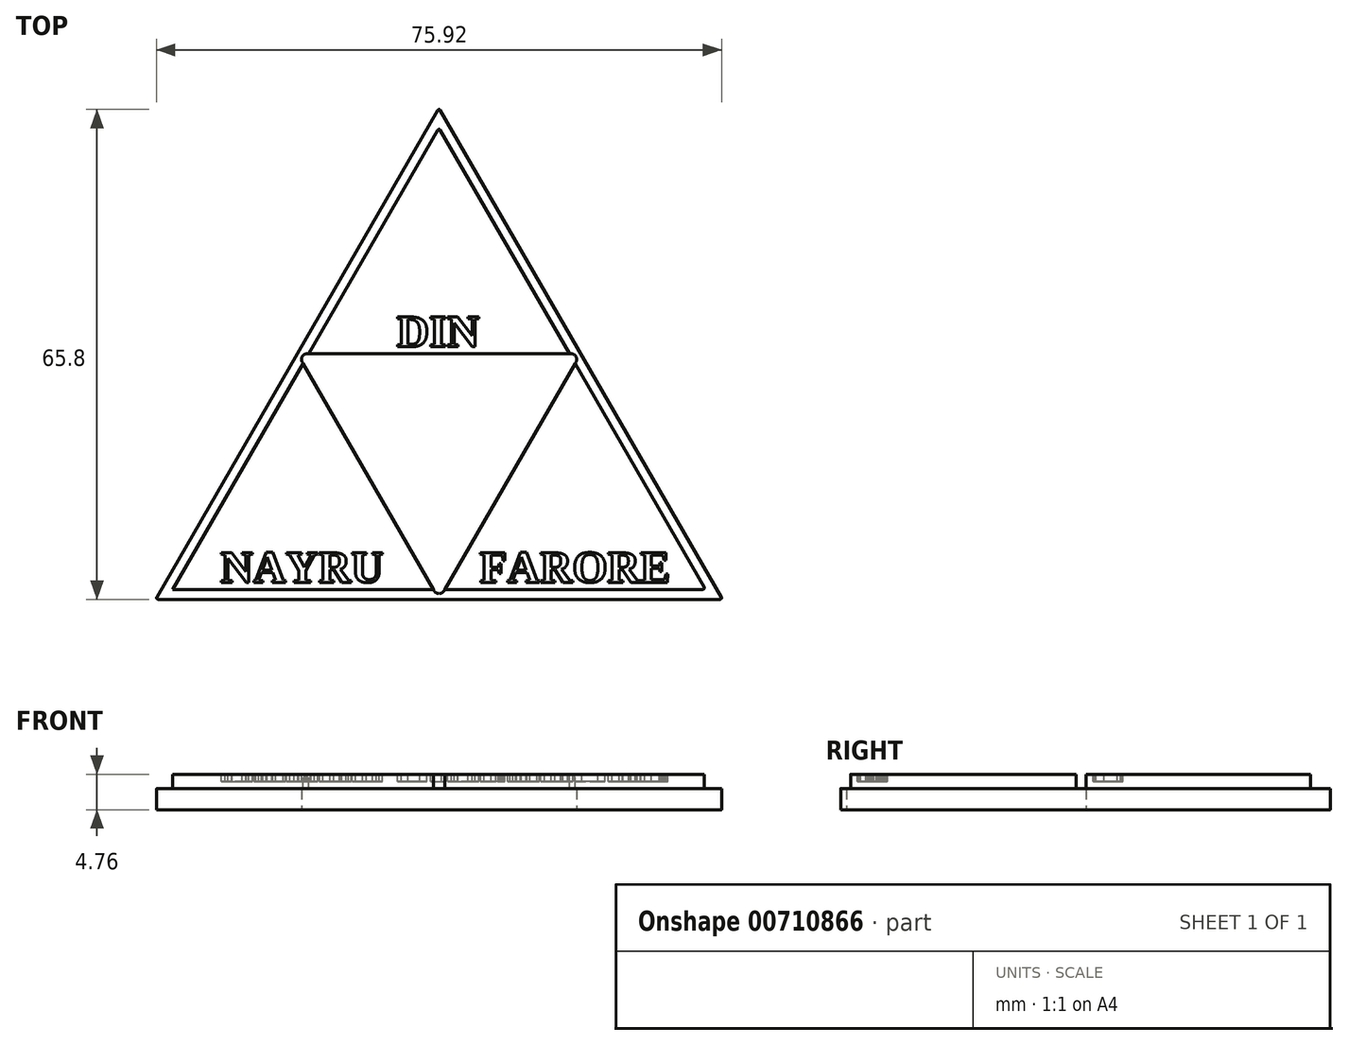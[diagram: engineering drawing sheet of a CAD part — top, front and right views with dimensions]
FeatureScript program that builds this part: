
annotation { "Feature Type Name" : "Feature", "Feature Type Description" : "" }
export const myFeature = defineFeature(function(context is Context, id is Id, definition is map)
    precondition{}
    {
        {
            var Q0;
            Q0=qCreatedBy(makeId("Top.planeOp"),FACE);
            var sketch = newSketch(context, id + "F0", { "sketchPlane" : qUnion([Q0])});
            skLineSegment(sketch, "E0", {"start": v(-0.1, -0.2) * mm, "end": v(-12.7, -22) * mm});
            skLineSegment(sketch, "E1", {"start": v(-11.82, -22) * mm, "end": v(11.82, -22) * mm});
            skLineSegment(sketch, "E2", {"start": v(12.7, -22) * mm, "end": v(0.1, -0.2) * mm});
            skLineSegment(sketch, "E3", {"start": v(-12.7, -22) * mm, "end": v(-25.3, -43.8) * mm});
            skLineSegment(sketch, "E4", {"start": v(-25.18, -44) * mm, "end": v(0, -44) * mm});
            skLineSegment(sketch, "E5", {"start": v(-0.44, -43.23) * mm, "end": v(-12.26, -22.76) * mm});
            skLineSegment(sketch, "E6", {"start": v(0.44, -43.23) * mm, "end": v(12.26, -22.76) * mm});
            skLineSegment(sketch, "E7", {"start": v(25.3, -43.8) * mm, "end": v(12.7, -22) * mm});
            skLineSegment(sketch, "E8", {"start": v(0, -44) * mm, "end": v(25.18, -44) * mm});
            skPoint(sketch, "E9.visualSharp", {"position": v(-12.7, -22) * mm});
            skArc(sketch, "E9.filletArc", {"start": v(-11.82, -22) * mm, "mid": v(-12.26, -22.25) * mm, "end": v(-12.26, -22.76) * mm});
            skPoint(sketch, "E10.visualSharp", {"position": v(12.7, -22) * mm});
            skArc(sketch, "E10.filletArc", {"start": v(12.26, -22.76) * mm, "mid": v(12.26, -22.25) * mm, "end": v(11.82, -22) * mm});
            skPoint(sketch, "E11.visualSharp", {"position": v(0, -44) * mm});
            skArc(sketch, "E11.filletArc", {"start": v(-0.44, -43.23) * mm, "mid": v(0, -43.49) * mm, "end": v(0.44, -43.23) * mm});
            skPoint(sketch, "E12.visualSharp", {"position": v(0, 0) * mm});
            skArc(sketch, "E12.filletArc", {"start": v(0.01, -0.02) * mm, "mid": v(0, -0.01) * mm, "end": v(-0.01, -0.02) * mm});
            skPoint(sketch, "E13.visualSharp", {"position": v(25.4, -44) * mm});
            skArc(sketch, "E13.filletArc", {"start": v(25.18, -44) * mm, "mid": v(25.3, -43.93) * mm, "end": v(25.3, -43.8) * mm});
            skPoint(sketch, "E14.visualSharp", {"position": v(-25.4, -44) * mm});
            skArc(sketch, "E14.filletArc", {"start": v(-25.3, -43.8) * mm, "mid": v(-25.3, -43.93) * mm, "end": v(-25.18, -44) * mm});
            skArc(sketch, "E15.filletArc", {"start": v(0.1, -0.2) * mm, "mid": v(0, -0.13) * mm, "end": v(-0.1, -0.2) * mm});
            skSolve(sketch);
        }
        {
            var Q0;
            Q0=makeQuery(id+"F0.imprint","IMPRINT",FACE,{"disambiguationData":[TD([[makeQuery(id+"F0.imprint","IMPRINT",EDGE,{"derivedFrom":sQuery(id+"F0.wireOp",EDGE,"E0")}),1.0]])]});
            var Q1;
            Q1=makeQuery(id+"F0.imprint","IMPRINT",FACE,{"disambiguationData":[TD([[makeQuery(id+"F0.imprint","IMPRINT",EDGE,{"derivedFrom":sQuery(id+"F0.wireOp",EDGE,"E6")}),-1.0]])]});
            var Q2;
            Q2=makeQuery(id+"F0.imprint","IMPRINT",FACE,{"disambiguationData":[TD([[makeQuery(id+"F0.imprint","IMPRINT",EDGE,{"derivedFrom":sQuery(id+"F0.wireOp",EDGE,"E3")}),1.0]])]});
            extrude(context, id + "F1", {"entities" : qUnion([Q0, Q1, Q2]), "depth" : 3.17 * mm, "offsetDistance" : 25.4 * mm});
        }
        {
            var Q0;
            Q0=makeQuery(id+"F1.opExtrude","CAP_FACE",FACE,{"disambiguationData":[OSD([sQuery(id+"F0.wireOp",EDGE,"E0"),sQuery(id+"F0.wireOp",EDGE,"E1"),sQuery(id+"F0.wireOp",EDGE,"E2"),sQuery(id+"F0.wireOp",EDGE,"E3"),sQuery(id+"F0.wireOp",EDGE,"E4"),sQuery(id+"F0.wireOp",EDGE,"E5"),sQuery(id+"F0.wireOp",EDGE,"E6"),sQuery(id+"F0.wireOp",EDGE,"E7"),sQuery(id+"F0.wireOp",EDGE,"E8"),sQuery(id+"F0.wireOp",EDGE,"E9.filletArc"),sQuery(id+"F0.wireOp",EDGE,"E10.filletArc"),sQuery(id+"F0.wireOp",EDGE,"E11.filletArc"),sQuery(id+"F0.wireOp",EDGE,"E13.filletArc"),sQuery(id+"F0.wireOp",EDGE,"E14.filletArc"),sQuery(id+"F0.wireOp",EDGE,"E15.filletArc")])],"isStart":false});
            var sketch = newSketch(context, id + "F2", { "sketchPlane" : qUnion([Q0])});
            skLineSegment(sketch, "E16", {"start": v(0, 0) * mm, "end": v(-25.4, -44) * mm});
            skLineSegment(sketch, "E17", {"start": v(0, 0) * mm, "end": v(25.4, -44) * mm});
            skLineSegment(sketch, "E18", {"start": v(25.18, -44) * mm, "end": v(25.4, -44) * mm});
            skLineSegment(sketch, "E19.trimOffspring", {"start": v(25.4, -44) * mm, "end": v(-25.4, -44) * mm});
            skLineSegment(sketch, "E20.0", {"start": v(-23.64, -43.1) * mm, "end": v(23.64, -43.1) * mm});
            skLineSegment(sketch, "E20.1", {"start": v(-0.1, -1.97) * mm, "end": v(-23.75, -42.91) * mm});
            skLineSegment(sketch, "E20.2", {"start": v(23.75, -42.91) * mm, "end": v(0.1, -1.97) * mm});
            skLineSegment(sketch, "E21.trimOffspring", {"start": v(23.86, -43.1) * mm, "end": v(-23.86, -43.1) * mm});
            skLineSegment(sketch, "E22.trimOffspring", {"start": v(0, -1.78) * mm, "end": v(-23.86, -43.1) * mm});
            skPoint(sketch, "E23.visualSharp", {"position": v(0, -1.78) * mm});
            skArc(sketch, "E23.filletArc", {"start": v(0.1, -1.97) * mm, "mid": v(0, -1.9) * mm, "end": v(-0.1, -1.97) * mm});
            skPoint(sketch, "E24.visualSharp", {"position": v(23.86, -43.1) * mm});
            skArc(sketch, "E24.filletArc", {"start": v(23.64, -43.1) * mm, "mid": v(23.75, -43.04) * mm, "end": v(23.75, -42.91) * mm});
            skPoint(sketch, "E25.visualSharp", {"position": v(-23.86, -43.1) * mm});
            skArc(sketch, "E25.filletArc", {"start": v(-23.75, -42.91) * mm, "mid": v(-23.75, -43.04) * mm, "end": v(-23.64, -43.1) * mm});
            skSolve(sketch);
        }
        {
            var Q0;
            {var subQ8=sQuery(id+"F2.wireOp",EDGE,"E23.filletArc");Q0=makeQuery(id+"F2.imprint","IMPRINT",FACE,{"disambiguationData":[TD([[makeQuery(id+"F2.imprint","IMPRINT",EDGE,{"derivedFrom":subQ8}),-1.0]])]});}
            extrude(context, id + "F3", {"entities" : qUnion([Q0]), "operationType" : NewBodyOperationType.REMOVE, "oppositeDirection" : true, "depth" : 1.27 * mm, "offsetDistance" : 25.4 * mm});
        }
        {
            var Q0;
            {var subQ0=sQuery(id+"F0.wireOp",EDGE,"E1");Q0=makeQuery(id+"F3.boolean.opBoolean","SPLIT",FACE,{"disambiguationData":[TD([makeQuery(id+"F1.opExtrude","SWEPT_FACE",FACE,{"disambiguationData":[OSD([subQ0])]})])],"derivedFrom":makeQuery(id+"F1.opExtrude","CAP_FACE",FACE,{"disambiguationData":[OSD([sQuery(id+"F0.wireOp",EDGE,"E0"),subQ0,sQuery(id+"F0.wireOp",EDGE,"E2"),sQuery(id+"F0.wireOp",EDGE,"E3"),sQuery(id+"F0.wireOp",EDGE,"E4"),sQuery(id+"F0.wireOp",EDGE,"E5"),sQuery(id+"F0.wireOp",EDGE,"E6"),sQuery(id+"F0.wireOp",EDGE,"E7"),sQuery(id+"F0.wireOp",EDGE,"E8"),sQuery(id+"F0.wireOp",EDGE,"E9.filletArc"),sQuery(id+"F0.wireOp",EDGE,"E10.filletArc"),sQuery(id+"F0.wireOp",EDGE,"E11.filletArc"),sQuery(id+"F0.wireOp",EDGE,"E13.filletArc"),sQuery(id+"F0.wireOp",EDGE,"E14.filletArc"),sQuery(id+"F0.wireOp",EDGE,"E15.filletArc")])],"isStart":false})});}
            var sketch = newSketch(context, id + "F4", { "sketchPlane" : qUnion([Q0])});
            skText(sketch, "E26", { "text": "DIN", "fontName": "Tinos-Bold.ttf"});
            skText(sketch, "E27", { "text": "NAYRU", "fontName": "Tinos-Bold.ttf"});
            skPoint(sketch, "E28", {"position": v(-12.2, -19.41) * mm});
            skText(sketch, "E29", { "text": "FARORE", "fontName": "Tinos-Bold.ttf"});
            const initialGuessF4  = {"E26": [-0.00381, -0.02136, 1, 0, 0.00291], "E27": [-0.01957, -0.04247, 1, 0, 0.00291], "E29": [0.00363, -0.04247, 1, 0, 0.00291]};
            skSetInitialGuess(sketch, initialGuessF4);
            skSolve(sketch);
        }
        {
            var Q0;
            Q0 = qSketchRegion(id + "F4", true);
            extrude(context, id + "F5", {"entities" : qUnion([Q0]), "operationType" : NewBodyOperationType.REMOVE, "oppositeDirection" : true, "depth" : 0.64 * mm, "offsetDistance" : 25.4 * mm});
        }
        {
            var Q0;
            Q0=makeQuery(id+"F1.opExtrude","SWEPT_BODY",BODY,{"disambiguationData":[OSD([sQuery(id+"F0.wireOp",EDGE,"E0"),sQuery(id+"F0.wireOp",EDGE,"E1"),sQuery(id+"F0.wireOp",EDGE,"E2"),sQuery(id+"F0.wireOp",EDGE,"E3"),sQuery(id+"F0.wireOp",EDGE,"E4"),sQuery(id+"F0.wireOp",EDGE,"E5"),sQuery(id+"F0.wireOp",EDGE,"E6"),sQuery(id+"F0.wireOp",EDGE,"E7"),sQuery(id+"F0.wireOp",EDGE,"E8"),sQuery(id+"F0.wireOp",EDGE,"E9.filletArc"),sQuery(id+"F0.wireOp",EDGE,"E10.filletArc"),sQuery(id+"F0.wireOp",EDGE,"E11.filletArc"),sQuery(id+"F0.wireOp",EDGE,"E13.filletArc"),sQuery(id+"F0.wireOp",EDGE,"E14.filletArc"),sQuery(id+"F0.wireOp",EDGE,"E15.filletArc")])]});
            var Q1;
            Q1=qCreatedBy(makeId("Origin.pointOp"),VERTEX);
            transform(context, id + "F6", {"entities" : qUnion([Q0]), "transformType" : TransformType.SCALE_UNIFORMLY, "scale" : 1.5, "scalePoint" : qUnion([Q1]), "makeCopy" : false});
        }
    });
